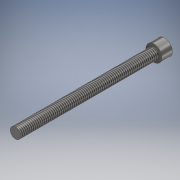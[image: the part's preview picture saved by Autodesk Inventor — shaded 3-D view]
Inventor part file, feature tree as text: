
AUTODESK INVENTOR PART (.ipt)
format: ipt  version: 2018 (Build 220112000, 112)  size: 116,224 bytes
history: native  units: mm
features: extrude x3, sketch x3, thread x1
ambient origin geometry x8: Origin, YZ Plane, XZ Plane, XY Plane, X Axis, Y Axis, Z Axis, Center Point
bodies: Solid1 (feature_tree)
feature tree (7):
  extrude  "Extrusion1"  Depth=52.0mm TaperAngle=0.0deg
  thread  "Thread1"  [1 undecoded]
  extrude  "Extrusion2"  Depth=4.0mm TaperAngle=0.0deg
  extrude  "Extrusion3"  [1 undecoded]
  sketch  "Sketch1"  dims[d0=4.0mm d1=52.0mm d2=0.0mm d3=10.0mm d4=0.0mm]
  sketch  "Sketch2"  dims[d5=6.0mm d6=4.0mm d7=0.0mm]
  sketch  "Sketch3"  dims[d8=3.0mm d9=0.0mm]
note: 2 required parameter values undecoded (feature->parameter linkage not recoverable at this tier; creation-order binding heuristic only, values carry confidence <= 0.55)
